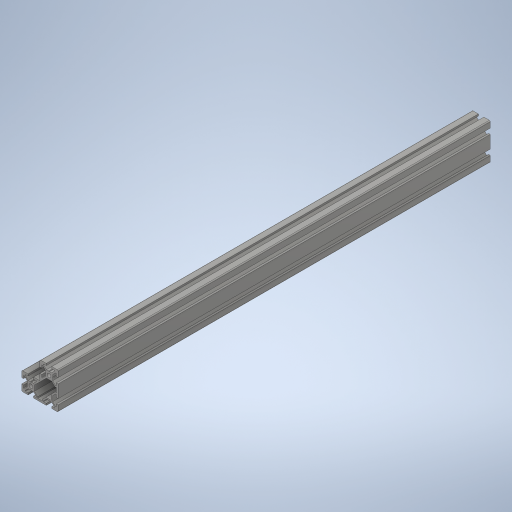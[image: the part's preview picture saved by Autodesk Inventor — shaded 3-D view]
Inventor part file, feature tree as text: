
AUTODESK INVENTOR PART (.ipt)
format: ipt  version: 2024 (Build 280153000, 153)  size: 448,000 bytes
history: native  units: mm
features: thread x4, sketch x3, hole x2, extrude x1
ambient origin geometry x8: Origin, YZ Plane, XZ Plane, XY Plane, X Axis, Y Axis, Z Axis, Center Point
bodies: Solid1 (feature_tree)
feature tree (10):
  extrude  "Extrusion1"  Depth=10.0mm TaperAngle=0.0deg
  hole  "Hole1"  [1 undecoded]
  hole  "Hole2"  [1 undecoded]
  thread  "Thread1"  [1 undecoded]
  thread  "Thread2"  [1 undecoded]
  thread  "Thread3"  [1 undecoded]
  thread  "Thread4"  [1 undecoded]
  sketch  "Sketch_1"  dims[d0=475.0mm d1=0.0mm]
  sketch  "Sketch2"  dims[d2=4.2mm d3=6.0mm d4=4.0mm d5=2.0mm d6=90.0deg d7=425.0mm d8=0.0mm]
  sketch  "Sketch3"  dims[d9=4.2mm d10=6.0mm d11=4.0mm d12=2.0mm d13=90.0deg d14=425.0mm d15=0.0mm d16=10.0mm d17=0.0mm d18=10.0mm d19=0.0mm d20=10.0mm d21=0.0mm d22=10.0mm d23=0.0mm]
note: 6 required parameter values undecoded (feature->parameter linkage not recoverable at this tier; creation-order binding heuristic only, values carry confidence <= 0.55)
